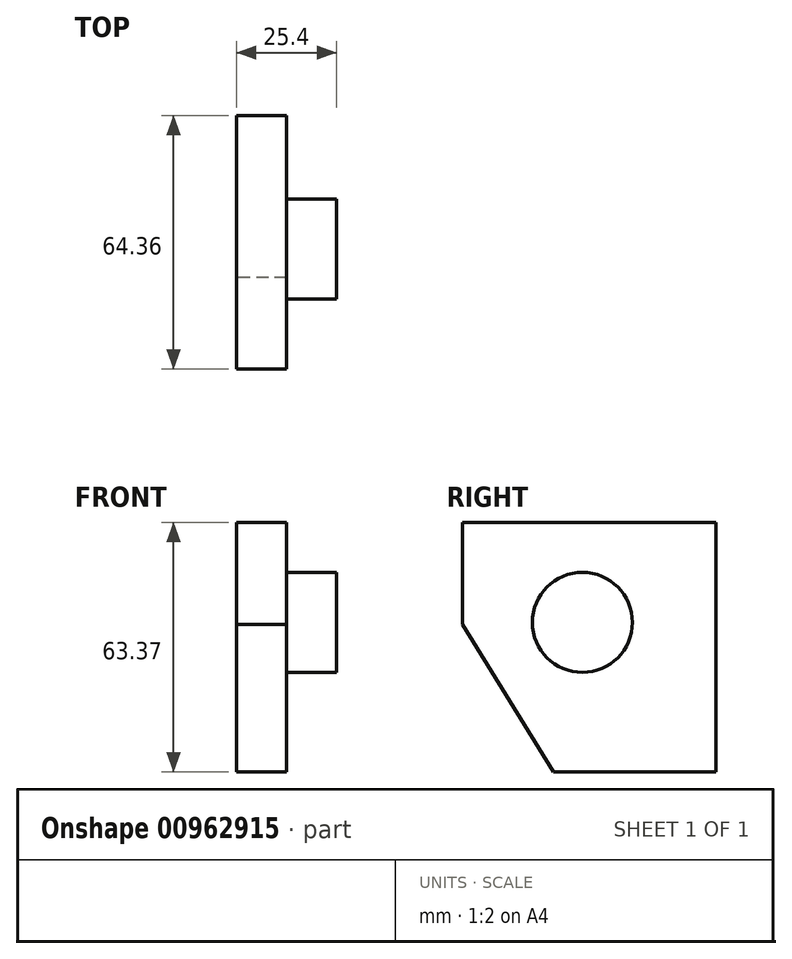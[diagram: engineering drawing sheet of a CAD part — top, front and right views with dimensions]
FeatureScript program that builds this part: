
annotation { "Feature Type Name" : "Feature", "Feature Type Description" : "" }
export const myFeature = defineFeature(function(context is Context, id is Id, definition is map)
    precondition{}
    {
        {
            var Q0;
            Q0=qCreatedBy(makeId("Right.planeOp"),FACE);
            var sketch = newSketch(context, id + "F0", { "sketchPlane" : qUnion([Q0])});
            skLineSegment(sketch, "E0", {"start": v(-40.94, 8.42) * mm, "end": v(-40.94, 34.36) * mm});
            skLineSegment(sketch, "E1", {"start": v(-40.94, 34.36) * mm, "end": v(23.42, 34.36) * mm});
            skLineSegment(sketch, "E2", {"start": v(23.42, 34.36) * mm, "end": v(23.42, -29.01) * mm});
            skLineSegment(sketch, "E3", {"start": v(23.42, -29.01) * mm, "end": v(-17.77, -29.01) * mm});
            skLineSegment(sketch, "E4", {"start": v(-17.77, -29.01) * mm, "end": v(-40.94, 8.42) * mm});
            skSolve(sketch);
        }
        {
            var Q0;
            Q0=makeQuery(id+"F0.imprint","IMPRINT",FACE,{"disambiguationData":[TD([[makeQuery(id+"F0.imprint","IMPRINT",EDGE,{"derivedFrom":sQuery(id+"F0.wireOp",EDGE,"E0")}),-1.0]])]});
            extrude(context, id + "F1", {"entities" : qUnion([Q0]), "depth" : 25.4 * mm, "offsetDistance" : 25.4 * mm});
        }
        {
            var Q0;
            Q0=makeQuery(id+"F1.opExtrude","CAP_FACE",FACE,{"disambiguationData":[OSD([sQuery(id+"F0.wireOp",EDGE,"E0"),sQuery(id+"F0.wireOp",EDGE,"E1"),sQuery(id+"F0.wireOp",EDGE,"E2"),sQuery(id+"F0.wireOp",EDGE,"E3"),sQuery(id+"F0.wireOp",EDGE,"E4")])],"isStart":false});
            var sketch = newSketch(context, id + "F2", { "sketchPlane" : qUnion([Q0])});
            skCircle(sketch, "E5", {"center": v(-10.46, 8.96) * mm, "radius": 12.7 * mm});
            skSolve(sketch);
        }
        {
            var Q0;
            Q0=makeQuery(id+"F2.imprint","IMPRINT",FACE,{"disambiguationData":[TD([[makeQuery(id+"F2.imprint","IMPRINT",EDGE,{"derivedFrom":sQuery(id+"F2.wireOp",EDGE,"E5")}),-1.0]])]});
            extrude(context, id + "F3", {"entities" : qUnion([Q0]), "operationType" : NewBodyOperationType.REMOVE, "oppositeDirection" : true, "depth" : 12.7 * mm, "offsetDistance" : 25.4 * mm});
        }
    });
